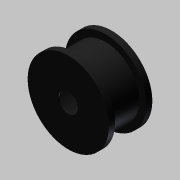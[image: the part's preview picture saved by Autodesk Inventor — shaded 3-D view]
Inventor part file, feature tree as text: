
AUTODESK INVENTOR PART (.ipt)
format: ipt  version: 2013 (Build 170138000, 138)  size: 120,320 bytes
history: native  units: in
note: dims shown in document units (in); Inventor stores cm internally (conversion verified against a paired STEP export)
features: extrude x4, sketch x4
ambient origin geometry x8: Origin, YZ Plane, XZ Plane, XY Plane, X Axis, Y Axis, Z Axis, Center Point
bodies: Solid1 (feature_tree)
feature tree (8):
  extrude  "Extrusion1"  Depth=0.1969in
  extrude  "Extrusion2"  Depth=0.8268in
  extrude  "Extrusion3"  Depth=0.8268in
  extrude  "Extrusion4"  Depth=0.6299in
  sketch  "Sketch1"  dims[d0=0.689in d1=0.1969in]
  sketch  "Sketch2"  dims[d2=0.315in d3=0.0in d4=0.8268in]
  sketch  "Sketch3"  dims[d5=0.063in d6=0.0in d7=0.8268in]
  sketch  "Sketch5"  dims[d8=0.063in d9=0.0in d11=0.6299in d12=0.4331in d13=0.0in]
